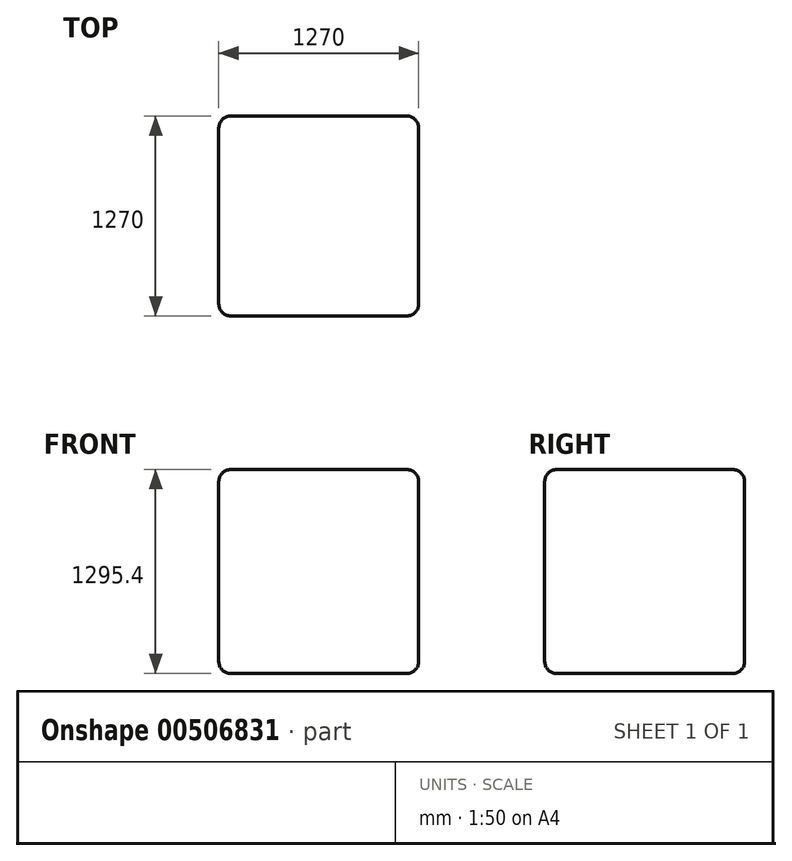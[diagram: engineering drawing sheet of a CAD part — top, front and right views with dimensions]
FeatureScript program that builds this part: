
annotation { "Feature Type Name" : "Feature", "Feature Type Description" : "" }
export const myFeature = defineFeature(function(context is Context, id is Id, definition is map)
    precondition{}
    {
        {
            var Q0;
            Q0=qCreatedBy(makeId("Top.planeOp"),FACE);
            var sketch = newSketch(context, id + "F0", { "sketchPlane" : qUnion([Q0])});
            skLineSegment(sketch, "E0.bottom", {"start": v(-635.05, 721.03) * mm, "end": v(634.95, 721.03) * mm});
            skLineSegment(sketch, "E0.top", {"start": v(-635.05, -548.97) * mm, "end": v(634.95, -548.97) * mm});
            skLineSegment(sketch, "E0.left", {"start": v(-635.05, 721.03) * mm, "end": v(-635.05, -548.97) * mm});
            skLineSegment(sketch, "E0.right", {"start": v(634.95, 721.03) * mm, "end": v(634.95, -548.97) * mm});
            skSolve(sketch);
        }
        {
            var Q0;
            Q0 = qSketchRegion(id + "F0", true);
            extrude(context, id + "F1", {"entities" : qUnion([Q0]), "depth" : 25.4 * mm});
        }
        {
            var Q0;
            Q0=makeQuery(id+"F0.imprint","IMPRINT",FACE,{"disambiguationData":[TD([[makeQuery(id+"F0.imprint","IMPRINT",EDGE,{"derivedFrom":sQuery(id+"F0.wireOp",EDGE,"E0.bottom")}),-1.0]])]});
            extrude(context, id + "F2", {"entities" : qUnion([Q0]), "operationType" : NewBodyOperationType.ADD, "oppositeDirection" : true, "depth" : 1270 * mm});
        }
        {
            var Q0;
            {var subQ0=sQuery(id+"F0.wireOp",EDGE,"E0.right");var subQ1=sQuery(id+"F0.wireOp",EDGE,"E0.top");Q0=makeQuery(id+"F2.boolean.opBoolean","MERGE",EDGE,{"derivedFrom":[makeQuery(id+"F1.opExtrude","SWEPT_EDGE",EDGE,{"disambiguationData":[OSD([subQ1,subQ0])]}),makeQuery(id+"F2.opExtrude","SWEPT_EDGE",EDGE,{"disambiguationData":[OSD([subQ1,subQ0])]})]});}
            var Q1;
            Q1=makeQuery(id+"F2.opExtrude","CAP_EDGE",EDGE,{"disambiguationData":[OSD([sQuery(id+"F0.wireOp",EDGE,"E0.top")])],"isStart":false});
            var Q2;
            Q2=makeQuery(id+"F1.opExtrude","CAP_EDGE",EDGE,{"disambiguationData":[OSD([sQuery(id+"F0.wireOp",EDGE,"E0.top")])],"isStart":false});
            var Q3;
            {var subQ0=sQuery(id+"F0.wireOp",EDGE,"E0.left");var subQ1=sQuery(id+"F0.wireOp",EDGE,"E0.top");Q3=makeQuery(id+"F2.boolean.opBoolean","MERGE",EDGE,{"derivedFrom":[makeQuery(id+"F1.opExtrude","SWEPT_EDGE",EDGE,{"disambiguationData":[OSD([subQ1,subQ0])]}),makeQuery(id+"F2.opExtrude","SWEPT_EDGE",EDGE,{"disambiguationData":[OSD([subQ1,subQ0])]})]});}
            var Q4;
            Q4=makeQuery(id+"F1.opExtrude","CAP_EDGE",EDGE,{"disambiguationData":[OSD([sQuery(id+"F0.wireOp",EDGE,"E0.right")])],"isStart":false});
            var Q5;
            Q5=makeQuery(id+"F1.opExtrude","CAP_EDGE",EDGE,{"disambiguationData":[OSD([sQuery(id+"F0.wireOp",EDGE,"E0.bottom")])],"isStart":false});
            var Q6;
            {var subQ0=sQuery(id+"F0.wireOp",EDGE,"E0.right");var subQ1=sQuery(id+"F0.wireOp",EDGE,"E0.bottom");Q6=makeQuery(id+"F2.boolean.opBoolean","MERGE",EDGE,{"derivedFrom":[makeQuery(id+"F1.opExtrude","SWEPT_EDGE",EDGE,{"disambiguationData":[OSD([subQ1,subQ0])]}),makeQuery(id+"F2.opExtrude","SWEPT_EDGE",EDGE,{"disambiguationData":[OSD([subQ1,subQ0])]})]});}
            var Q7;
            Q7=makeQuery(id+"F2.opExtrude","CAP_EDGE",EDGE,{"disambiguationData":[OSD([sQuery(id+"F0.wireOp",EDGE,"E0.right")])],"isStart":false});
            var Q8;
            Q8=makeQuery(id+"F1.opExtrude","CAP_EDGE",EDGE,{"disambiguationData":[OSD([sQuery(id+"F0.wireOp",EDGE,"E0.left")])],"isStart":false});
            var Q9;
            Q9=makeQuery(id+"F2.opExtrude","CAP_EDGE",EDGE,{"disambiguationData":[OSD([sQuery(id+"F0.wireOp",EDGE,"E0.left")])],"isStart":false});
            var Q10;
            {var subQ0=sQuery(id+"F0.wireOp",EDGE,"E0.left");var subQ1=sQuery(id+"F0.wireOp",EDGE,"E0.bottom");Q10=makeQuery(id+"F2.boolean.opBoolean","MERGE",EDGE,{"derivedFrom":[makeQuery(id+"F1.opExtrude","SWEPT_EDGE",EDGE,{"disambiguationData":[OSD([subQ1,subQ0])]}),makeQuery(id+"F2.opExtrude","SWEPT_EDGE",EDGE,{"disambiguationData":[OSD([subQ1,subQ0])]})]});}
            var Q11;
            Q11=makeQuery(id+"F2.opExtrude","CAP_EDGE",EDGE,{"disambiguationData":[OSD([sQuery(id+"F0.wireOp",EDGE,"E0.bottom")])],"isStart":false});
            fillet(context, id + "F3", {"entities" : qUnion([Q0, Q1, Q2, Q3, Q4, Q5, Q6, Q7, Q8, Q9, Q10, Q11]), "radius" : 76.2 * mm, "tangentPropagation" : true, "allowEdgeOverflow" : false});
        }
    });
